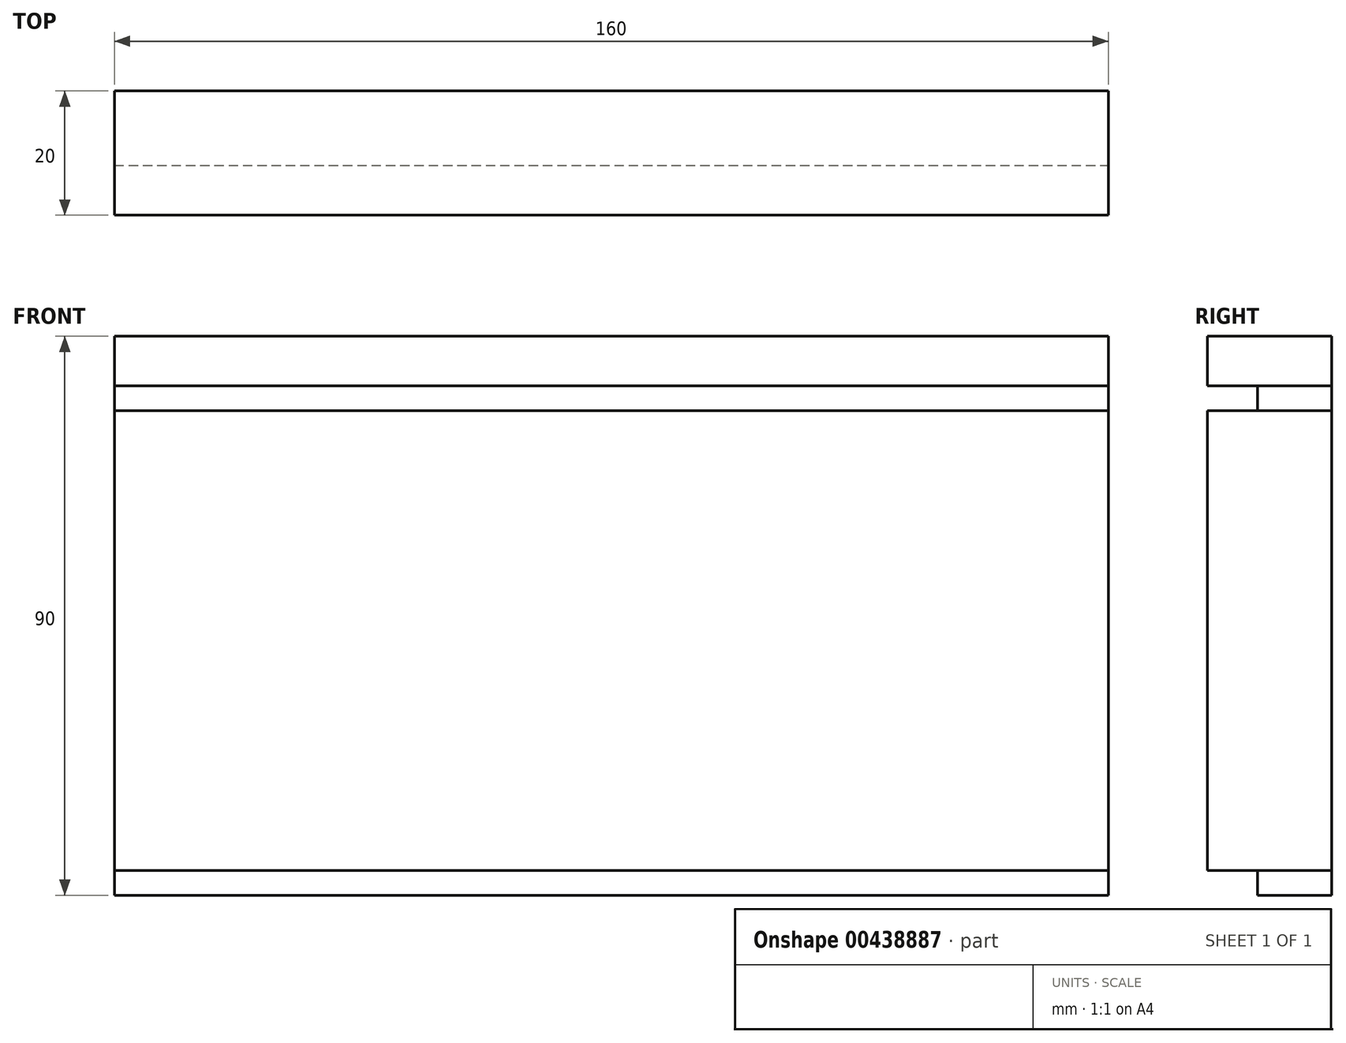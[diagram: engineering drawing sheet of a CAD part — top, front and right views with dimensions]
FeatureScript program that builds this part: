
annotation { "Feature Type Name" : "Feature", "Feature Type Description" : "" }
export const myFeature = defineFeature(function(context is Context, id is Id, definition is map)
    precondition{}
    {
        {
            var Q0;
            Q0=qCreatedBy(makeId("Front.planeOp"),FACE);
            var sketch = newSketch(context, id + "F0", { "sketchPlane" : qUnion([Q0])});
            skLineSegment(sketch, "E0.bottom", {"start": v(80, 45) * mm, "end": v(-80, 45) * mm});
            skLineSegment(sketch, "E0.top", {"start": v(80, -45) * mm, "end": v(-80, -45) * mm});
            skLineSegment(sketch, "E0.left", {"start": v(80, 45) * mm, "end": v(80, -45) * mm});
            skLineSegment(sketch, "E0.right", {"start": v(-80, 45) * mm, "end": v(-80, -45) * mm});
            skPoint(sketch, "E0.middle", {"position": v(0, 0) * mm});
            skLineSegment(sketch, "E1", {"start": v(-80, 37) * mm, "end": v(80, 37) * mm});
            skLineSegment(sketch, "E2", {"start": v(-80, 33) * mm, "end": v(80, 33) * mm});
            skLineSegment(sketch, "E3", {"start": v(-80, -41) * mm, "end": v(80, -41) * mm});
            skSolve(sketch);
        }
        {
            var Q0;
            {var subQ0=sQuery(id+"F0.wireOp",EDGE,"E0.top");Q0=makeQuery(id+"F0.imprint","IMPRINT",FACE,{"disambiguationData":[TD([[makeQuery(id+"F0.imprint","IMPRINT",EDGE,{"derivedFrom":subQ0}),-1.0]])]});}
            var Q1;
            {var subQ0=sQuery(id+"F0.wireOp",EDGE,"E1");Q1=makeQuery(id+"F0.imprint","IMPRINT",FACE,{"disambiguationData":[TD([[makeQuery(id+"F0.imprint","IMPRINT",EDGE,{"derivedFrom":subQ0}),-1.0]])]});}
            extrude(context, id + "F1", {"entities" : qUnion([Q0, Q1]), "depth" : 12 * mm});
        }
        {
            var Q0;
            {var subQ0=sQuery(id+"F0.wireOp",EDGE,"E0.bottom");Q0=makeQuery(id+"F0.imprint","IMPRINT",FACE,{"disambiguationData":[TD([[makeQuery(id+"F0.imprint","IMPRINT",EDGE,{"derivedFrom":subQ0}),1.0]])]});}
            var Q1;
            {var subQ0=sQuery(id+"F0.wireOp",EDGE,"E2");Q1=makeQuery(id+"F0.imprint","IMPRINT",FACE,{"disambiguationData":[TD([[makeQuery(id+"F0.imprint","IMPRINT",EDGE,{"derivedFrom":subQ0}),-1.0]])]});}
            extrude(context, id + "F2", {"entities" : qUnion([Q0, Q1]), "depth" : 20 * mm});
        }
    });
